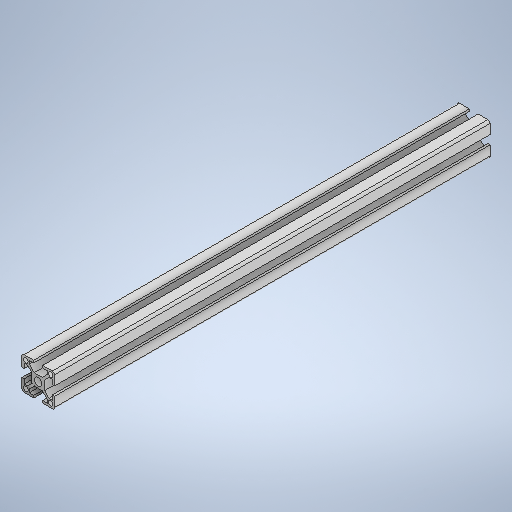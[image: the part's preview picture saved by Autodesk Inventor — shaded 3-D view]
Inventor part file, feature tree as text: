
AUTODESK INVENTOR PART (.ipt)
format: ipt  version: 2025 (Build 290162000, 162)  size: 312,832 bytes
history: native  units: in
note: dims shown in document units (in); Inventor stores cm internally (conversion verified against a paired STEP export)
features: extrude x1, sketch x1
ambient origin geometry x8: Origin, YZ Plane, XZ Plane, XY Plane, X Axis, Y Axis, Z Axis, Center Point
bodies: Solid1 (feature_tree)
feature tree (2):
  extrude  "Extrusion1"  Depth=15.748in
  sketch  "Sketch1"  dims[d6=15.748in d7=0.0in d8=0.1969in d9=0.0344in d10=0.1969in d11=0.0344in]
